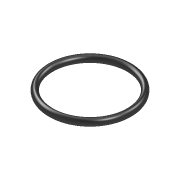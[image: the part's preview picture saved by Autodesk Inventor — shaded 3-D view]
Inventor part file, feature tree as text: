
AUTODESK INVENTOR PART (.ipt)
format: ipt  version: 2022.3 (Build 263350000, 350)  size: 135,680 bytes
history: native  units: mm
features: sketch x2, other x1, sweep x1
ambient origin geometry x8: Origin, YZ Plane, XZ Plane, XY Plane, X Axis, Y Axis, Z Axis, Center Point
bodies: Body1 (feature_tree)
feature tree (4):
  other  "Sólido1"
  sweep  "Barrido1"
  sketch  "Boceto1"  dims[d0=2.0mm d1=1.65mm]
  sketch  "Boceto2"  dims[d2=21.75mm d3=0.0mm d4=0.0mm]
